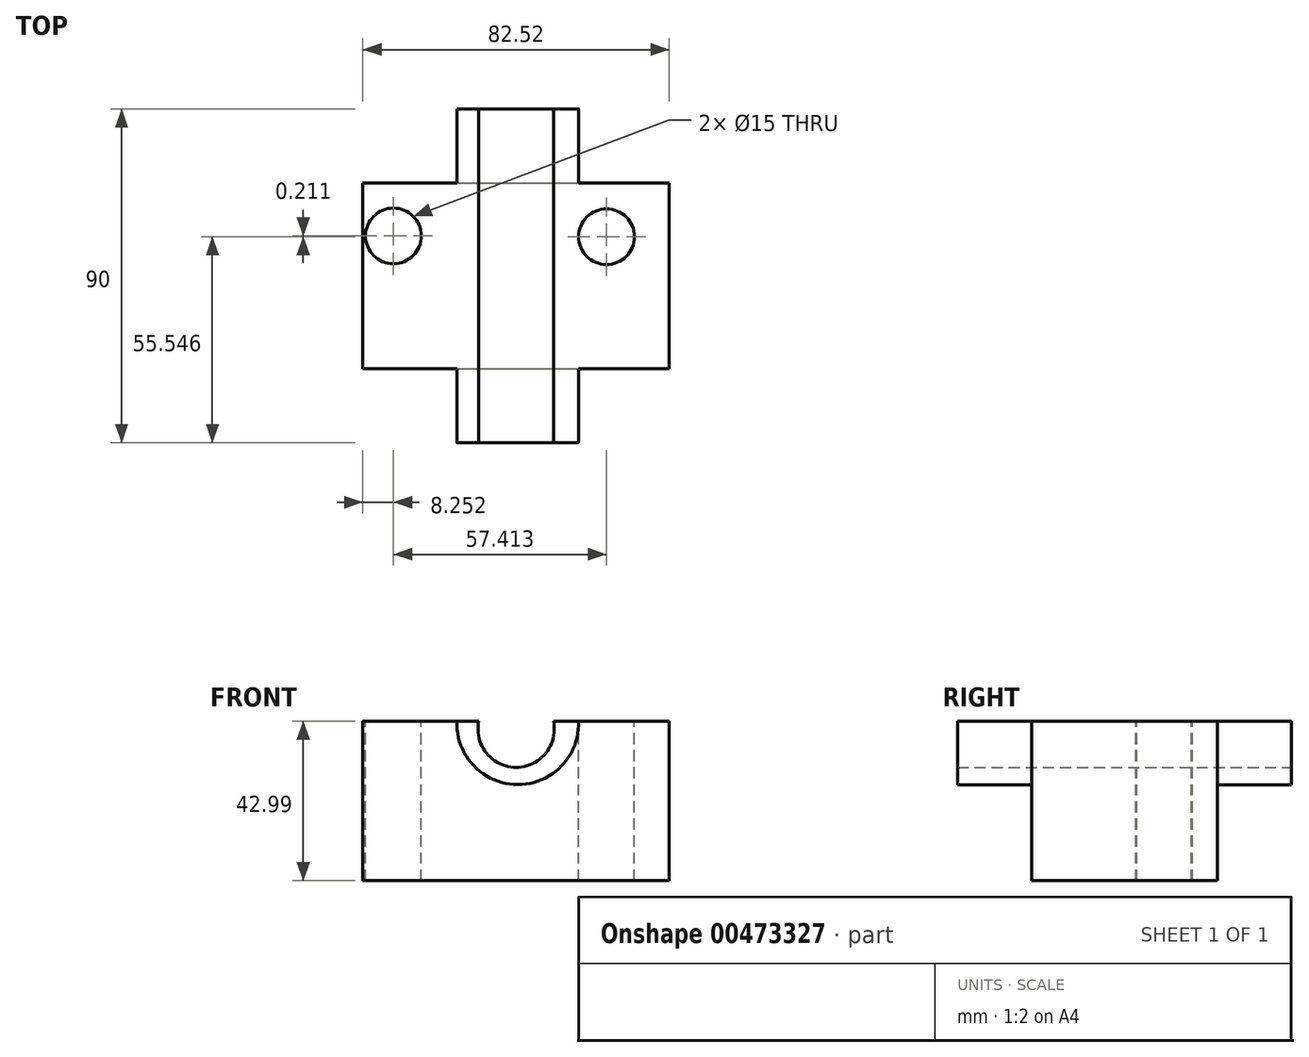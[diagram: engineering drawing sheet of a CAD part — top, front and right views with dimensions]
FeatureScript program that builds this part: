
annotation { "Feature Type Name" : "Feature", "Feature Type Description" : "" }
export const myFeature = defineFeature(function(context is Context, id is Id, definition is map)
    precondition{}
    {
        {
            var Q0;
            Q0=qCreatedBy(makeId("Front.planeOp"),FACE);
            var sketch = newSketch(context, id + "F0", { "sketchPlane" : qUnion([Q0])});
            skLineSegment(sketch, "E0.bottom", {"start": v(-39.84, 31.98) * mm, "end": v(42.68, 31.98) * mm});
            skLineSegment(sketch, "E0.top", {"start": v(-39.84, -11.01) * mm, "end": v(42.68, -11.01) * mm});
            skLineSegment(sketch, "E0.left", {"start": v(-39.84, 31.98) * mm, "end": v(-39.84, -11.01) * mm});
            skLineSegment(sketch, "E0.right", {"start": v(42.68, 31.98) * mm, "end": v(42.68, -11.01) * mm});
            skArc(sketch, "E1", {"start": v(-14.46, 31.98) * mm, "mid": v(1.91, 14.88) * mm, "end": v(18.3, 31.98) * mm});
            skArc(sketch, "E2", {"start": v(-8.59, 31.98) * mm, "mid": v(1.48, 19.55) * mm, "end": v(11.54, 31.98) * mm});
            skSolve(sketch);
        }
        {
            var Q0;
            Q0=makeQuery(id+"F0.imprint","IMPRINT",FACE,{"disambiguationData":[TD([[makeQuery(id+"F0.imprint","IMPRINT",EDGE,{"derivedFrom":sQuery(id+"F0.wireOp",EDGE,"E0.top")}),1.0]])]});
            extrude(context, id + "F1", {"entities" : qUnion([Q0]), "depth" : 50 * mm});
        }
        {
            var Q0;
            {var subQ0=sQuery(id+"F0.wireOp",EDGE,"E1");Q0=makeQuery(id+"F0.imprint","IMPRINT",FACE,{"disambiguationData":[TD([[makeQuery(id+"F0.imprint","IMPRINT",EDGE,{"derivedFrom":subQ0}),1.0]])]});}
            extrude(context, id + "F2", {"entities" : qUnion([Q0]), "operationType" : NewBodyOperationType.ADD, "depth" : 70 * mm, "hasSecondDirection" : true, "secondDirectionOppositeDirection" : true, "secondDirectionDepth" : 20 * mm});
        }
        {
            var Q0;
            Q0=qCreatedBy(makeId("Top.planeOp"),FACE);
            var sketch = newSketch(context, id + "F3", { "sketchPlane" : qUnion([Q0])});
            skCircle(sketch, "E3", {"center": v(-31.59, -14.24) * mm, "radius": 3.41 * mm});
            skCircle(sketch, "E4", {"center": v(25.83, -14.45) * mm, "radius": 3.92 * mm});
            skSolve(sketch);
        }
        {
            var Q0;
            Q0=sQuery(id+"F3.wireOp",VERTEX,"E3.center");
            var Q1;
            Q1=makeQuery(id+"F1.opExtrude","SWEPT_BODY",BODY,{"disambiguationData":[OSD([sQuery(id+"F0.wireOp",EDGE,"E0.bottom"),sQuery(id+"F0.wireOp",EDGE,"E0.top"),sQuery(id+"F0.wireOp",EDGE,"E0.left"),sQuery(id+"F0.wireOp",EDGE,"E0.right"),sQuery(id+"F0.wireOp",EDGE,"E1")])]});
            hole(context, id + "F4", {"style" : HoleStyle.SIMPLE, "endStyle" : HoleEndStyle.THROUGH, "holeDiameter" : 15 * mm, "isTappedThrough" : true, "tappedDepth" : 12 * mm, "tapClearance" : 3, "locations" : qUnion([Q0]), "scope" : qUnion([Q1])});
        }
        {
            var Q0;
            Q0=sQuery(id+"F3.wireOp",VERTEX,"E3.center");
            var Q1;
            Q1=makeQuery(id+"F1.opExtrude","SWEPT_BODY",BODY,{"disambiguationData":[OSD([sQuery(id+"F0.wireOp",EDGE,"E0.bottom"),sQuery(id+"F0.wireOp",EDGE,"E0.top"),sQuery(id+"F0.wireOp",EDGE,"E0.left"),sQuery(id+"F0.wireOp",EDGE,"E0.right"),sQuery(id+"F0.wireOp",EDGE,"E1")])]});
            hole(context, id + "F5", {"style" : HoleStyle.SIMPLE, "endStyle" : HoleEndStyle.THROUGH, "oppositeDirection" : true, "holeDiameter" : 15 * mm, "isTappedThrough" : true, "tappedDepth" : 12 * mm, "tapClearance" : 3, "locations" : qUnion([Q0]), "scope" : qUnion([Q1])});
        }
        {
            var Q0;
            Q0=sQuery(id+"F3.wireOp",VERTEX,"E4.center");
            var Q1;
            Q1=makeQuery(id+"F1.opExtrude","SWEPT_BODY",BODY,{"disambiguationData":[OSD([sQuery(id+"F0.wireOp",EDGE,"E0.bottom"),sQuery(id+"F0.wireOp",EDGE,"E0.top"),sQuery(id+"F0.wireOp",EDGE,"E0.left"),sQuery(id+"F0.wireOp",EDGE,"E0.right"),sQuery(id+"F0.wireOp",EDGE,"E1")])]});
            hole(context, id + "F6", {"style" : HoleStyle.SIMPLE, "endStyle" : HoleEndStyle.THROUGH, "holeDiameter" : 15 * mm, "isTappedThrough" : true, "tappedDepth" : 12 * mm, "tapClearance" : 3, "locations" : qUnion([Q0]), "scope" : qUnion([Q1])});
        }
        {
            var Q0;
            Q0=sQuery(id+"F3.wireOp",VERTEX,"E4.center");
            var Q1;
            Q1=makeQuery(id+"F1.opExtrude","SWEPT_BODY",BODY,{"disambiguationData":[OSD([sQuery(id+"F0.wireOp",EDGE,"E0.bottom"),sQuery(id+"F0.wireOp",EDGE,"E0.top"),sQuery(id+"F0.wireOp",EDGE,"E0.left"),sQuery(id+"F0.wireOp",EDGE,"E0.right"),sQuery(id+"F0.wireOp",EDGE,"E1")])]});
            hole(context, id + "F7", {"style" : HoleStyle.SIMPLE, "endStyle" : HoleEndStyle.THROUGH, "oppositeDirection" : true, "holeDiameter" : 15 * mm, "isTappedThrough" : true, "tappedDepth" : 12 * mm, "tapClearance" : 3, "locations" : qUnion([Q0]), "scope" : qUnion([Q1])});
        }
    });
